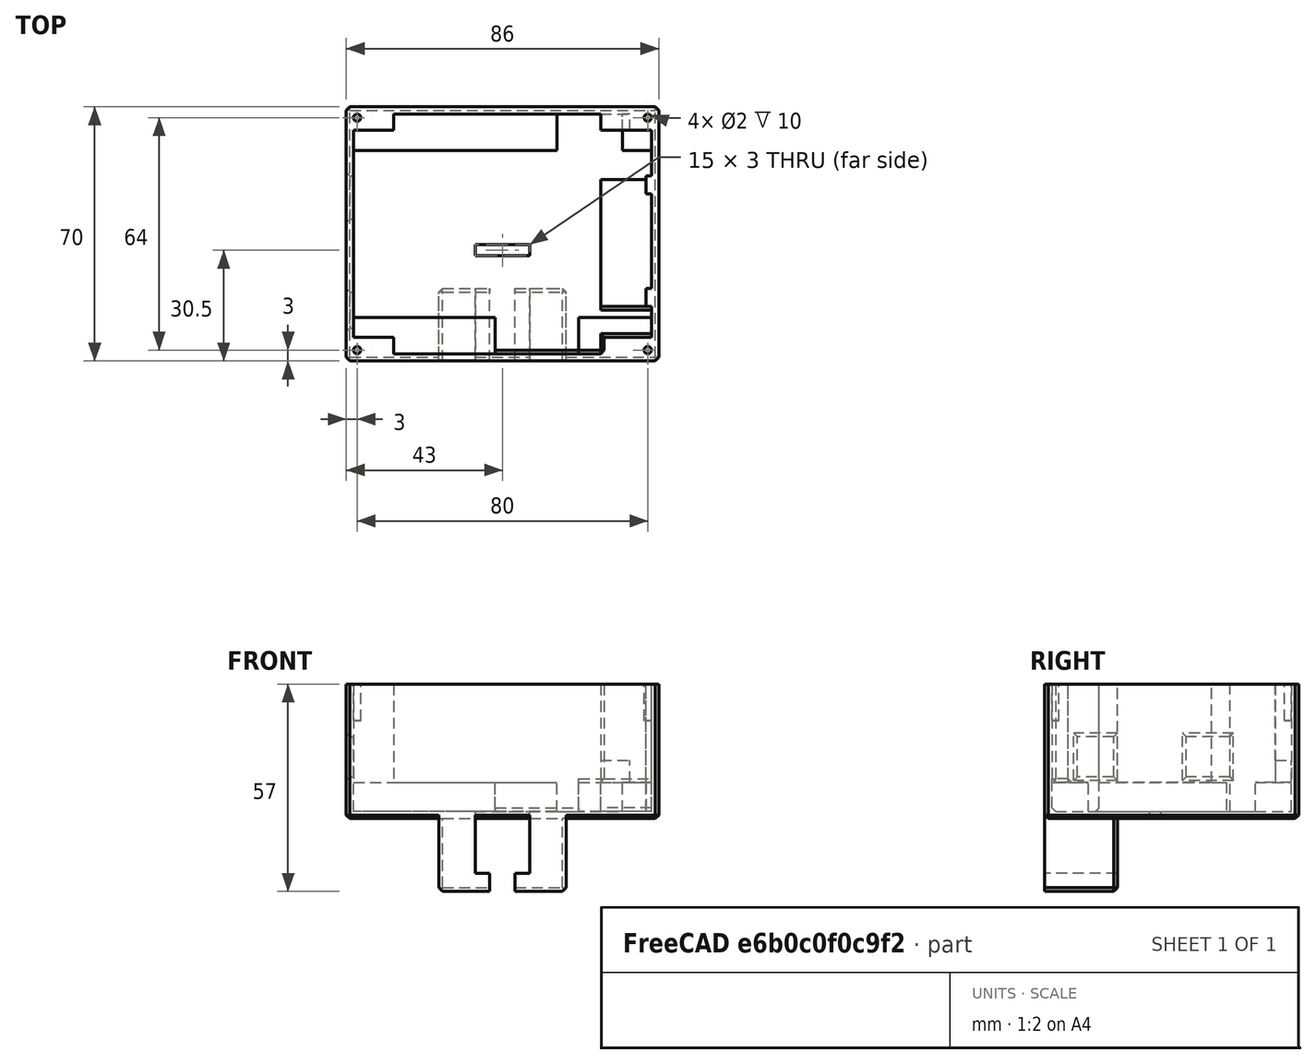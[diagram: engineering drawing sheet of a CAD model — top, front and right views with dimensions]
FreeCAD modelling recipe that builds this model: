
FCSTD DOCUMENT  (FreeCAD 0.19RUnknown)
Label: caja_base_01
License: All rights reserved
LicenseURL: http://en.wikipedia.org/wiki/All_rights_reserved
objects: Part::Box×24, Part::Cut×10, Part::Cylinder×4, Part::MultiFuse×1, Part::Refine×1, Part::Chamfer×1
note: 41 computed .brp shape members not serialized (recipe doc carries the construction recipe); baked Part::Feature solids carry a one-line shape summary decoded from their .brp

FEATURE [Part::Box] Box  label="Cubo"
  AttacherType = Attacher::AttachEngine3D
  Height = 2
  Length = 86
  Width = 70
FEATURE [Part::Box] Box001  label="Cubo001"
  AttacherType = Attacher::AttachEngine3D
  Height = 37
  Length = 86
  Width = 2
FEATURE [Part::Box] Box002  label="Cubo002"
  AttacherType = Attacher::AttachEngine3D
  Height = 37
  Length = 86
  Placement = pos=(0,68,0) rot=(0,0,1;0rad)
  Width = 2
FEATURE [Part::Box] Box003  label="Cubo003"
  AttacherType = Attacher::AttachEngine3D
  Height = 37
  Length = 2
  Width = 70
FEATURE [Part::Box] Box004  label="Cubo004"
  AttacherType = Attacher::AttachEngine3D
  Height = 37
  Length = 2
  Placement = pos=(84,0,0) rot=(0,0,1;0rad)
  Width = 70
FEATURE [Part::Box] Box005  label="Cubo005"
  AttacherType = Attacher::AttachEngine3D
  Height = 37
  Length = 13
  Width = 6.5
FEATURE [Part::Box] Box006  label="Cubo006"
  AttacherType = Attacher::AttachEngine3D
  Height = 37
  Length = 15
  Placement = pos=(71,0,0) rot=(0,0,1;0rad)
  Width = 6.5
FEATURE [Part::Box] Box007  label="Cubo007"
  AttacherType = Attacher::AttachEngine3D
  Height = 37
  Length = 13
  Placement = pos=(0,63.5,0) rot=(0,0,1;0rad)
  Width = 6.5
FEATURE [Part::Box] Box008  label="Cubo008"
  AttacherType = Attacher::AttachEngine3D
  Height = 37
  Length = 16
  Placement = pos=(70,63.5,0) rot=(0,0,1;0rad)
  Width = 6.5
FEATURE [Part::Box] Box009  label="Cubo009"
  AttacherType = Attacher::AttachEngine3D
  Height = 11
  Length = 10
  Placement = pos=(-1,9,11.5) rot=(0,0,1;0rad)
  Width = 10
FEATURE [Part::Box] Box010  label="Cubo010"
  AttacherType = Attacher::AttachEngine3D
  Height = 11
  Length = 16
  Placement = pos=(-1,39,11.5) rot=(0,0,1;0rad)
  Width = 12
FEATURE [Part::Cylinder] Cylinder  label="Cilindro"
  Angle = 360
  AttacherType = Attacher::AttachEngine3D
  Height = 10
  Placement = pos=(3,3,27) rot=(0,0,1;0rad)
  Radius = 1
FEATURE [Part::Cylinder] Cylinder001  label="Cilindro001"
  Angle = 360
  AttacherType = Attacher::AttachEngine3D
  Height = 10
  Placement = pos=(3,67,27) rot=(0,0,1;0rad)
  Radius = 1
FEATURE [Part::Cylinder] Cylinder002  label="Cilindro002"
  Angle = 360
  AttacherType = Attacher::AttachEngine3D
  Height = 10
  Placement = pos=(83,3,27) rot=(0,0,1;0rad)
  Radius = 1
FEATURE [Part::Cylinder] Cylinder003  label="Cilindro003"
  Angle = 360
  AttacherType = Attacher::AttachEngine3D
  Height = 10
  Placement = pos=(83,67,27) rot=(0,0,1;0rad)
  Radius = 1
FEATURE [Part::Cut] Cut002
  Base = -> Box005
  Tool = -> Cylinder
FEATURE [Part::Cut] Cut003
  Base = -> Box007
  Tool = -> Cylinder001
FEATURE [Part::Cut] Cut004
  Base = -> Box006
  Tool = -> Cylinder002
FEATURE [Part::Cut] Cut005
  Base = -> Box008
  Tool = -> Cylinder003
FEATURE [Part::Cut] Cut
  Base = -> Box003
  Tool = -> Box010
FEATURE [Part::Cut] Cut006
  Base = -> Cut
  Tool = -> Box009
FEATURE [Part::Box] Box016  label="Cubo016"
  AttacherType = Attacher::AttachEngine3D
  Height = 10
  Length = 86
  Width = 12
FEATURE [Part::Box] Box017  label="Cubo017"
  AttacherType = Attacher::AttachEngine3D
  Height = 10
  Length = 86
  Placement = pos=(0,58,0) rot=(0,0,1;0rad)
  Width = 12
FEATURE [Part::Box] Box018  label="Cubo018"
  AttacherType = Attacher::AttachEngine3D
  Height = 10
  Length = 15
  Placement = pos=(70,15,0) rot=(0,0,1;0rad)
  Width = 35
FEATURE [Part::Box] Box019  label="Cubo019"
  AttacherType = Attacher::AttachEngine3D
  Height = 20
  Length = 10
  Placement = pos=(25.5,0,-20) rot=(0,0,1;0rad)
  Width = 20
FEATURE [Part::Box] Box020  label="Cubo020"
  AttacherType = Attacher::AttachEngine3D
  Height = 20
  Length = 10
  Placement = pos=(50.5,0,-20) rot=(0,0,1;0rad)
  Width = 20
FEATURE [Part::Box] Box021  label="Cubo021"
  AttacherType = Attacher::AttachEngine3D
  Height = 5
  Length = 14
  Placement = pos=(25.5,0,-20) rot=(0,0,1;0rad)
  Width = 20
FEATURE [Part::Box] Box022  label="Cubo022"
  AttacherType = Attacher::AttachEngine3D
  Height = 5
  Length = 14
  Placement = pos=(46.5,0,-20) rot=(0,0,1;0rad)
  Width = 20
FEATURE [Part::Box] Box023  label="Cubo023"
  AttacherType = Attacher::AttachEngine3D
  Height = 37
  Length = 1.5
  Placement = pos=(82.5,15,0) rot=(0,0,1;0rad)
  Width = 5
FEATURE [Part::Box] Box024  label="Cubo024"
  AttacherType = Attacher::AttachEngine3D
  Height = 37
  Length = 1.5
  Placement = pos=(82.5,46,0) rot=(0,0,1;0rad)
  Width = 5
FEATURE [Part::Box] Box025  label="Cubo025"
  AttacherType = Attacher::AttachEngine3D
  Height = 8
  Length = 23
  Placement = pos=(41,2,2) rot=(0,0,1;0rad)
  Width = 10
FEATURE [Part::Cut] Cut007
  Base = -> Box016
  Tool = -> Box025
FEATURE [Part::Box] Box026  label="Cubo026"
  AttacherType = Attacher::AttachEngine3D
  Height = 8
  Length = 18
  Placement = pos=(58,58,2) rot=(0,0,1;0rad)
  Width = 10
FEATURE [Part::Cut] Cut008
  Base = -> Box017
  Tool = -> Box026
FEATURE [Part::Box] Box027  label="Cubo027"
  AttacherType = Attacher::AttachEngine3D
  Height = 14
  Length = 8
  Placement = pos=(70,63,2) rot=(0,0,1;0rad)
  Width = 5
FEATURE [Part::Cut] Cut009
  Base = -> Cut005
  Tool = -> Box027
FEATURE [Part::MultiFuse] Fusion
  Shapes = -> [Box,Box001,Box002,Box004,Cut002,Cut003,Cut004,Cut006,Box018,Box019,Box020,Box021,Box022,Box023,Box024,Cut007,Cut008,Cut009]
FEATURE [Part::Refine] Fusion001
  Source = -> Fusion
FEATURE [Part::Chamfer] Chamfer
  Base = -> Fusion001
  Edges = 30 edges r=1: [Edge30,Edge33,Edge39,Edge40,Edge42,Edge53,Edge56,Edge59,Edge61,Edge76,Edge78,Edge80,Edge81,Edge109,Edge110,Edge111,Edge112,Edge182,Edge183,Edge184,Edge185,Edge195,Edge196,Edge197,Edge198,Edge199,Edge200,Edge201,Edge202,Edge203]
FEATURE [Part::Box] Box028  label="Cubo028"
  AttacherType = Attacher::AttachEngine3D
  Height = 3
  Length = 15
  Placement = pos=(35.5,29,-1) rot=(0,0,1;0rad)
  Width = 3
FEATURE [Part::Cut] Cut010
  Base = -> Chamfer
  Refine = true
  Tool = -> Box028
